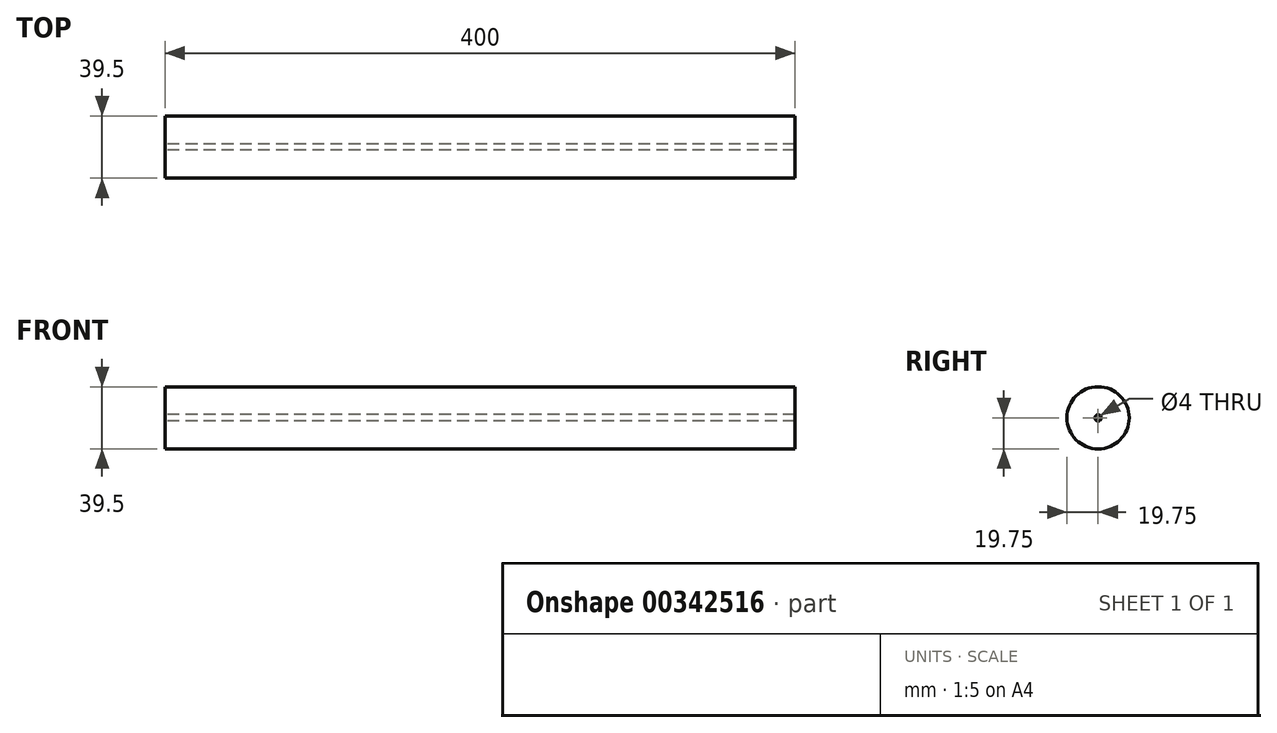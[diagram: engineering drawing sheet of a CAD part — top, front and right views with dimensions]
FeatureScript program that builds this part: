
annotation { "Feature Type Name" : "Feature", "Feature Type Description" : "" }
export const myFeature = defineFeature(function(context is Context, id is Id, definition is map)
    precondition{}
    {
        {
            var Q0;
            Q0=qCreatedBy(makeId("Right.planeOp"),FACE);
            var sketch = newSketch(context, id + "F0", { "sketchPlane" : qUnion([Q0])});
            skCircle(sketch, "E0", {"center": v(0, 0) * mm, "radius": 19.75 * mm});
            skCircle(sketch, "E1", {"center": v(0, 0) * mm, "radius": 2 * mm});
            skSolve(sketch);
        }
        {
            var Q0;
            Q0=makeQuery(id+"F0.imprint","IMPRINT",FACE,{"disambiguationData":[TD([[makeQuery(id+"F0.imprint","IMPRINT",EDGE,{"derivedFrom":sQuery(id+"F0.wireOp",EDGE,"E0")}),1.0]])]});
            extrude(context, id + "F1", {"entities" : qUnion([Q0]), "depth" : 400 * mm});
        }
    });
